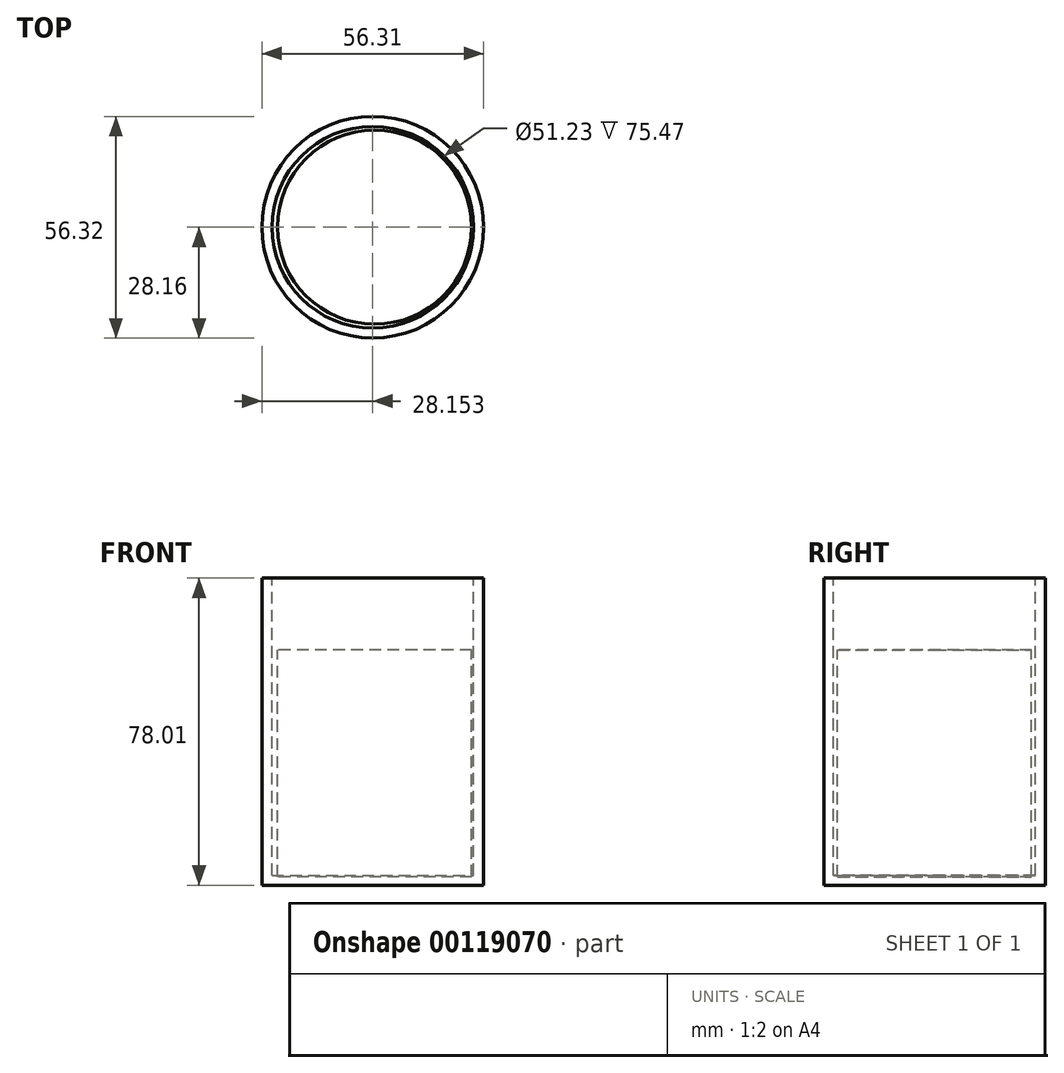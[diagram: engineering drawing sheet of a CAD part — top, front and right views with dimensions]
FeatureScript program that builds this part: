
annotation { "Feature Type Name" : "Feature", "Feature Type Description" : "" }
export const myFeature = defineFeature(function(context is Context, id is Id, definition is map)
    precondition{}
    {
        {
            var Q0;
            Q0=qCreatedBy(makeId("Front.planeOp"),FACE);
            var sketch = newSketch(context, id + "F0", { "sketchPlane" : qUnion([Q0])});
            skLineSegment(sketch, "E0.bottom", {"start": v(-12.92, 18.23) * mm, "end": v(15.23, 18.23) * mm});
            skLineSegment(sketch, "E0.top", {"start": v(-12.92, -59.78) * mm, "end": v(15.23, -59.78) * mm});
            skLineSegment(sketch, "E0.left", {"start": v(-12.92, 18.23) * mm, "end": v(-12.92, -59.78) * mm});
            skLineSegment(sketch, "E0.right", {"start": v(15.23, 18.23) * mm, "end": v(15.23, -59.78) * mm});
            skLineSegment(sketch, "E1", {"start": v(-12.92, -7.15) * mm, "end": v(-29.08, -7.15) * mm});
            skLineSegment(sketch, "E2", {"start": v(-29.08, -7.15) * mm, "end": v(-29.08, -33) * mm});
            skLineSegment(sketch, "E3", {"start": v(-29.08, -33) * mm, "end": v(-12.92, -33) * mm});
            skSolve(sketch);
        }
        {
            var Q0;
            Q0=makeQuery(id+"F0.imprint","IMPRINT",FACE,{"disambiguationData":[TD([[makeQuery(id+"F0.imprint","IMPRINT",EDGE,{"derivedFrom":sQuery(id+"F0.wireOp",EDGE,"E0.bottom")}),-1.0]])]});
            var Q1;
            Q1=sQuery(id+"F0.wireOp",EDGE,"E0.right");
            revolve(context, id + "F1", {"entities" : qUnion([Q0]), "axis" : qUnion([Q1]), "revolveType" : RevolveType.FULL});
        }
        {
            var Q0;
            Q0=makeQuery(id+"F1.opRevolve","SWEPT_FACE",FACE,{"disambiguationData":[OSD([sQuery(id+"F0.wireOp",EDGE,"E0.bottom")])]});
            shell(context, id + "F2", {"entities" : qUnion([Q0]), "thickness" : 2.54 * mm});
        }
        {
            var Q0;
            Q0=qCreatedBy(makeId("Top.planeOp"),FACE);
            var sketch = newSketch(context, id + "F3", { "sketchPlane" : qUnion([Q0])});
            skCircle(sketch, "E4", {"center": v(15.7, 0) * mm, "radius": 24.66 * mm});
            skSolve(sketch);
        }
        {
            var Q0;
            Q0=makeQuery(id+"F3.imprint","IMPRINT",FACE,{"disambiguationData":[TD([[makeQuery(id+"F3.imprint","IMPRINT",EDGE,{"derivedFrom":sQuery(id+"F3.wireOp",EDGE,"E4")}),1.0]])]});
            extrude(context, id + "F4", {"entities" : qUnion([Q0]), "oppositeDirection" : true, "depth" : 57.64 * mm});
        }
    });
